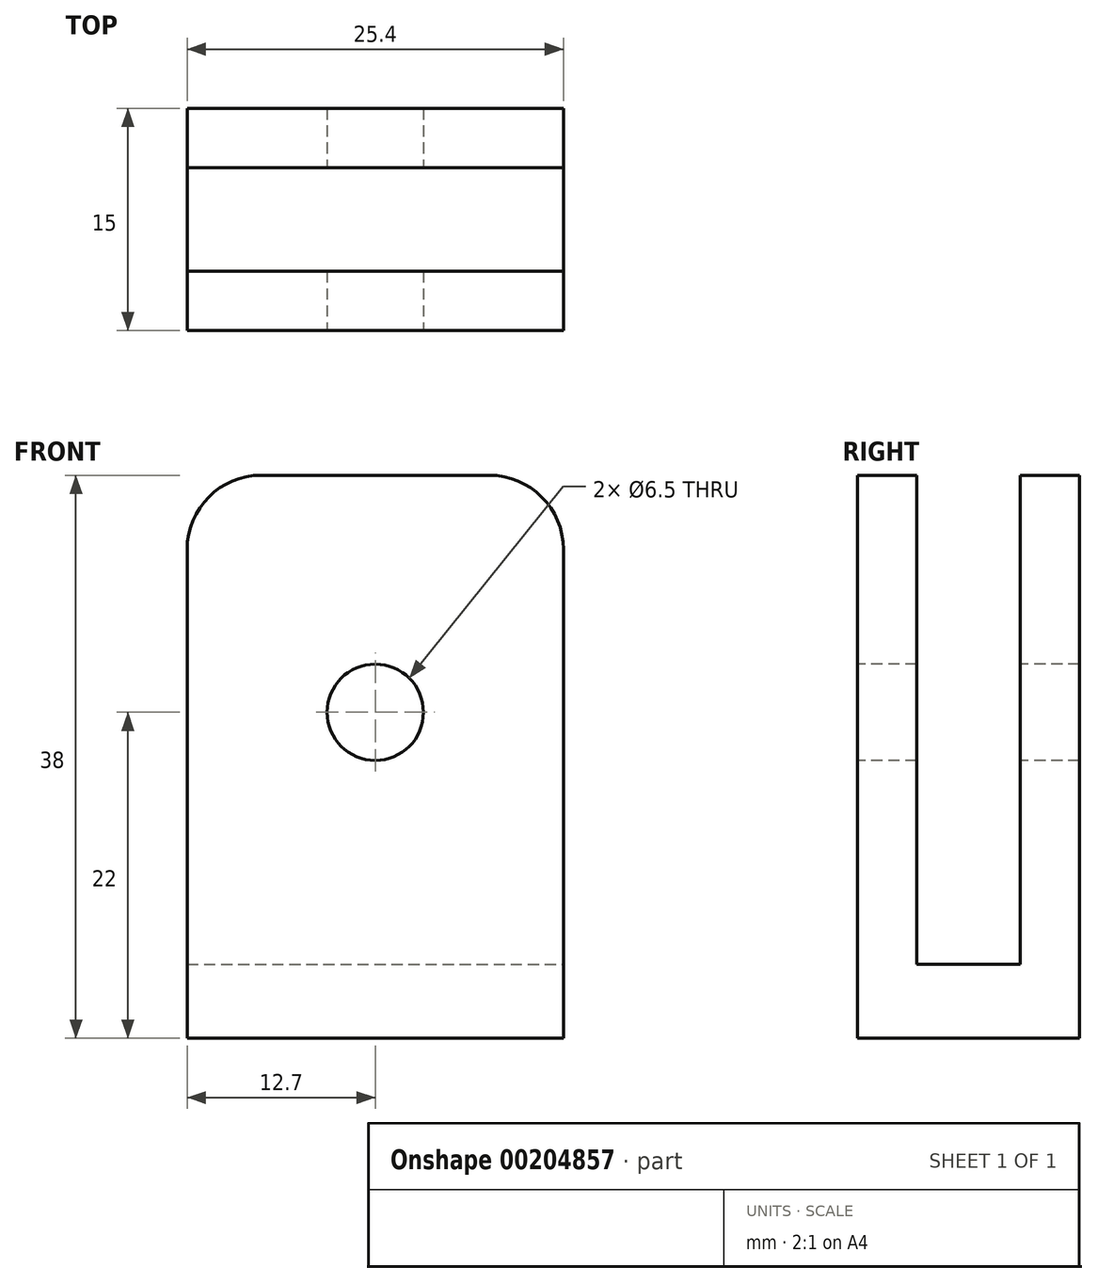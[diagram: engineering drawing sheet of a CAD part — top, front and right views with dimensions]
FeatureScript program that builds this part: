
annotation { "Feature Type Name" : "Feature", "Feature Type Description" : "" }
export const myFeature = defineFeature(function(context is Context, id is Id, definition is map)
    precondition{}
    {
        {
            var Q0;
            Q0=qCreatedBy(makeId("Top.planeOp"),FACE);
            var sketch = newSketch(context, id + "F0", { "sketchPlane" : qUnion([Q0])});
            skLineSegment(sketch, "E0.bottom", {"start": v(-12.7, 7.5) * mm, "end": v(12.7, 7.5) * mm});
            skLineSegment(sketch, "E0.top", {"start": v(-12.7, -7.5) * mm, "end": v(12.7, -7.5) * mm});
            skLineSegment(sketch, "E0.left", {"start": v(-12.7, 7.5) * mm, "end": v(-12.7, -7.5) * mm});
            skLineSegment(sketch, "E0.right", {"start": v(12.7, 7.5) * mm, "end": v(12.7, -7.5) * mm});
            skSolve(sketch);
        }
        {
            var Q0;
            Q0=makeQuery(id+"F0.imprint","IMPRINT",FACE,{"disambiguationData":[TD([[makeQuery(id+"F0.imprint","IMPRINT",EDGE,{"derivedFrom":sQuery(id+"F0.wireOp",EDGE,"E0.bottom")}),-1.0]])]});
            extrude(context, id + "F1", {"entities" : qUnion([Q0]), "depth" : 38 * mm});
        }
        {
            var Q0;
            Q0=makeQuery(id+"F1.opExtrude","SWEPT_FACE",FACE,{"disambiguationData":[OSD([sQuery(id+"F0.wireOp",EDGE,"E0.right")])]});
            var sketch = newSketch(context, id + "F2", { "sketchPlane" : qUnion([Q0])});
            skLineSegment(sketch, "E1.bottom", {"start": v(-3.5, 38) * mm, "end": v(3.5, 38) * mm});
            skLineSegment(sketch, "E1.top", {"start": v(-3.5, 5) * mm, "end": v(3.5, 5) * mm});
            skLineSegment(sketch, "E1.left", {"start": v(-3.5, 38) * mm, "end": v(-3.5, 5) * mm});
            skLineSegment(sketch, "E1.right", {"start": v(3.5, 38) * mm, "end": v(3.5, 5) * mm});
            skSolve(sketch);
        }
        {
            var Q0;
            Q0=makeQuery(id+"F2.imprint","IMPRINT",FACE,{"disambiguationData":[TD([[makeQuery(id+"F2.imprint","IMPRINT",EDGE,{"derivedFrom":sQuery(id+"F2.wireOp",EDGE,"E1.bottom")}),1.0]])]});
            extrude(context, id + "F3", {"entities" : qUnion([Q0]), "operationType" : NewBodyOperationType.REMOVE, "endBound" : BoundingType.UP_TO_NEXT, "oppositeDirection" : true, "depth" : 25 * mm});
        }
        {
            var Q0;
            {var subQ0=sQuery(id+"F0.wireOp",EDGE,"E0.bottom");var subQ1=sQuery(id+"F0.wireOp",EDGE,"E0.right");Q0=makeQuery(id+"F3.boolean.opBoolean","SPLIT",EDGE,{"disambiguationData":[TD([makeQuery(id+"F1.opExtrude","SWEPT_FACE",FACE,{"disambiguationData":[OSD([subQ0])]})])],"derivedFrom":makeQuery(id+"F1.opExtrude","CAP_EDGE",EDGE,{"disambiguationData":[OSD([subQ1])],"isStart":false})});}
            var Q1;
            {var subQ0=sQuery(id+"F0.wireOp",EDGE,"E0.bottom");var subQ1=sQuery(id+"F0.wireOp",EDGE,"E0.left");Q1=makeQuery(id+"F3.boolean.opBoolean","SPLIT",EDGE,{"disambiguationData":[TD([makeQuery(id+"F1.opExtrude","SWEPT_FACE",FACE,{"disambiguationData":[OSD([subQ0])]})])],"derivedFrom":makeQuery(id+"F1.opExtrude","CAP_EDGE",EDGE,{"disambiguationData":[OSD([subQ1])],"isStart":false})});}
            var Q2;
            {var subQ0=sQuery(id+"F0.wireOp",EDGE,"E0.left");var subQ1=sQuery(id+"F0.wireOp",EDGE,"E0.top");Q2=makeQuery(id+"F3.boolean.opBoolean","SPLIT",EDGE,{"disambiguationData":[TD([makeQuery(id+"F1.opExtrude","SWEPT_FACE",FACE,{"disambiguationData":[OSD([subQ1])]})])],"derivedFrom":makeQuery(id+"F1.opExtrude","CAP_EDGE",EDGE,{"disambiguationData":[OSD([subQ0])],"isStart":false})});}
            var Q3;
            {var subQ0=sQuery(id+"F0.wireOp",EDGE,"E0.right");var subQ1=sQuery(id+"F0.wireOp",EDGE,"E0.top");Q3=makeQuery(id+"F3.boolean.opBoolean","SPLIT",EDGE,{"disambiguationData":[TD([makeQuery(id+"F1.opExtrude","SWEPT_FACE",FACE,{"disambiguationData":[OSD([subQ1])]})])],"derivedFrom":makeQuery(id+"F1.opExtrude","CAP_EDGE",EDGE,{"disambiguationData":[OSD([subQ0])],"isStart":false})});}
            fillet(context, id + "F4", {"entities" : qUnion([Q0, Q1, Q2, Q3]), "radius" : 5 * mm, "tangentPropagation" : true, "allowEdgeOverflow" : false});
        }
        {
            var Q0;
            Q0=makeQuery(id+"F1.opExtrude","SWEPT_FACE",FACE,{"disambiguationData":[OSD([sQuery(id+"F0.wireOp",EDGE,"E0.top")])]});
            var sketch = newSketch(context, id + "F5", { "sketchPlane" : qUnion([Q0])});
            skCircle(sketch, "E2", {"center": v(0, 22) * mm, "radius": 3.25 * mm});
            skSolve(sketch);
        }
        {
            var Q0;
            Q0 = qSketchRegion(id + "F5", true);
            extrude(context, id + "F6", {"entities" : qUnion([Q0]), "operationType" : NewBodyOperationType.REMOVE, "oppositeDirection" : true, "depth" : 25 * mm});
        }
    });
